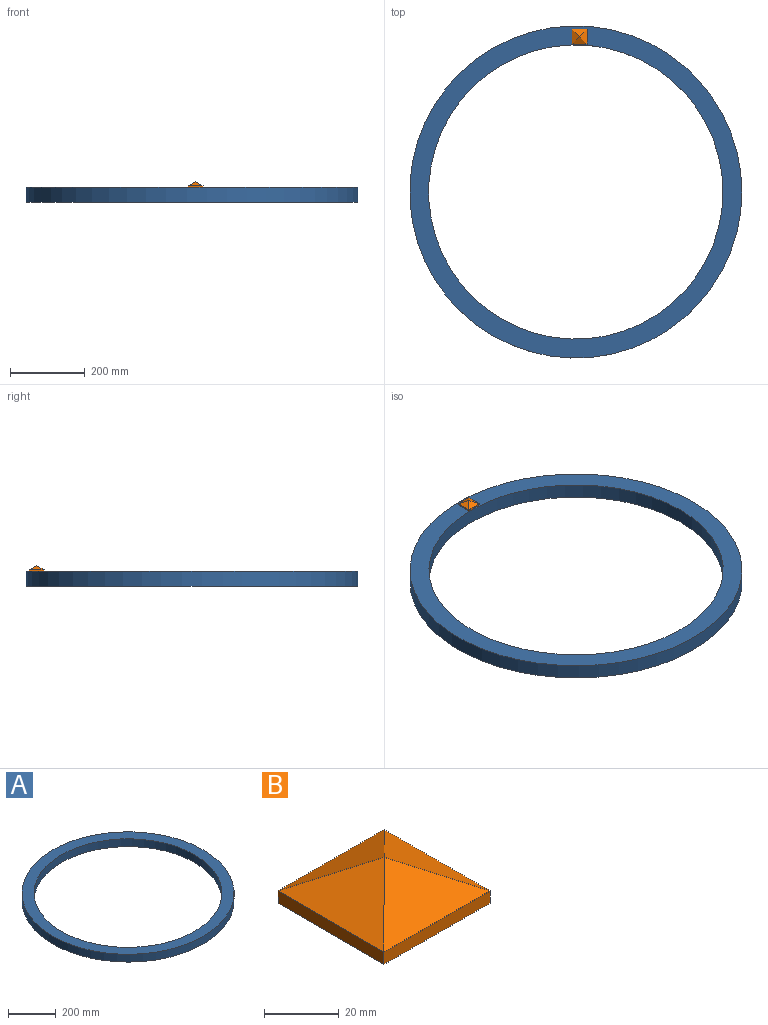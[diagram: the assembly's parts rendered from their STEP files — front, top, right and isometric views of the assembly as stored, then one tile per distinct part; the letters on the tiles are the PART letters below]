
ASSEMBLY  parts=2 mates=1
PART A: 4 faces, bbox 891.7x891.7x40 mm
  f0: cylinder r=445.86mm len=891.71mm, axis (0,0,-1), area 112055.6mm2, adj f1,f2
  f1: plane 891.71x891.71mm, normal (0,0,1), area 134339.8mm2, adj f0,f3
  f2: plane 891.71x891.71mm, normal (0,0,-1), area 134339.8mm2, adj f0,f3
  f3: cylinder r=395mm len=790mm, axis (0,0,1), area 99274.3mm2, adj f1,f2
PART B: 9 faces, bbox 40x40x15 mm
  f0: plane 40x4mm, normal (0,-1,0), area 160mm2, adj f1,f3,f4,f7
  f1: plane 40x4mm, normal (1,0,0), area 160mm2, adj f0,f2,f4,f8
  f2: plane 40x4mm, normal (0,1,0), area 160mm2, adj f1,f3,f4,f5
  f3: plane 40x4mm, normal (-1,0,0), area 160mm2, adj f0,f2,f4,f6
  f4: plane 40x40mm, normal (0,0,-1), area 1600mm2, adj f0,f1,f2,f3
  f5: plane 40x20mm, normal (0,0.48,0.88), area 456.5mm2, adj f2,f6,f8
  f6: plane 40x20mm, normal (-0.48,0,0.88), area 456.5mm2, adj f3,f5,f7
  f7: plane 40x20mm, normal (0,-0.48,0.88), area 456.5mm2, adj f0,f6,f8
  f8: plane 40x20mm, normal (0.48,0,0.88), area 456.5mm2, adj f1,f5,f7
PLACE A at identity
PLACE B t=(10,417,40)mm
MATE parallel B.f4 <-> A.f0  axis (0,0,1) through (30,397,40)mm
